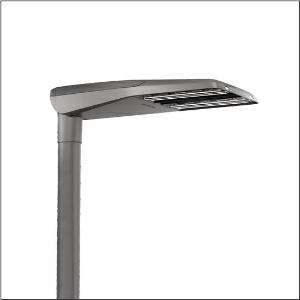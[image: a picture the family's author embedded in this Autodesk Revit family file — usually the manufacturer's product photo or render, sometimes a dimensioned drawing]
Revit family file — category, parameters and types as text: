
# Revit family: streetlight_sl_11_iq_midi___pc-l_5xc3e41e08me_b69f
name_source: partatom
category: Lighting Fixtures
units: mm (PartAtom-declared; Revit-internal decimal feet)

## family parameters
Cut with Voids When Loaded = No
Host = Face
Light Source = No
Part Type = Normal
Room Calculation Point = No
Round Connector Dimension = Use Diameter
Shared = No

## types (1)
- --- (1 x LED, 16220 lm, 124.7 W, 4000K)
    Apparent Load = 125 VA
    CIE Flux Codes = 37 73 96 100 100
    Color Rendering = 70
    Color Temperature = 4000K
    Default Elevation = 1800 mm
    Description = Streetlight SL 11 iQ midi, mast luminaire, primary light control with 3 zone facetted reflector, of plastic, silver coated, highly specular, primary optical cover: cover, of PMMA, transparent, light distribution: PC-L, light emission: direct distribution, primary light characteristic: asymmetric, left, installation type: post-top, side-entry, LED, High Power LED, rated luminous flux: 16.220lm, luminous efficacy: 130lm/W, light colour: 740, colour temperature: 4000K, control: optimised constant luminous flux control (CLO 2.0), Desk-Remote (wireless, voltage-free reading and setting of iQ features in the workshop via application-optimized NFC function/RFID function), Light-Fading, Smart-Wire, Night-Set, Lumen-Switch, Temp-Guard, Auto-Match, with cable H07RN-F 5x 1.5mm², mains connection: 230..240V, AC, 50/60Hz, connection cable pre-assembled, cable length: 12,5m, start of lifetime: 125W, end of service life: 132W, reduction: 57W, luminaire housing, of diecast aluminium, powder-coated, Siteco® metallic grey (DB 702S), please order mast flange separately, inclination adjustable without tools: 0°, 5°, 10°, 15° (post-top) | 0°, -5°, -10°, -15° (side-entry), sealing non-destructively replaceable, multi-level sealing system, length: 780mm, width: 376mm, height: 118mm, mast flange for spigot size: 42mm (side-entry): 5XC10008XM4, 60/48mm (side-entry/post-top): 5XC10108XM2, 76/60mm (side-entry/post-top): 5XC10108XM1, equipment: Power, protection rating (complete): IP66, insulation class (complete): insulation class II (safety insulation), certification: CE, ENEC, VDE, impact resistance: IK09, permissible operating ambient temperature for outdoor applications: -25..+50°C, standard-compliant lighting for roads and squares, Environmental Product Declaration (EPD) tested and certified by an independent institute, packaging unit: 1 piece

Light Distribution: PC-L
    Height = 118 mm
    Lamp = 1 x LED
    Lamp Light Flux = 16220 lm
    Lamp Power = 124.7 W
    Lamp count = 1
    Length = 780 mm
    Luminous efficacy = 130 lm/W
    Manufacturer = Siteco
    ModVariant = No
    Model = 5XC3E41E08ME
    Number of Poles = 1
    OnlyDefault = Yes
    Power Factor = 1
    Product Name = Streetlight SL 11 iQ midi | PC-L
    Product group = mast luminaire | pylon top
    ProductGroupID = 6100
    Protection Class = Protection class II
    Protection Degree = IP 66
    RLX_Detail_Level = 1
    RLX_Emergency_Light_Flux = 0 lm
    RLX_Emergency_Type = 0
    RLX_Emergency_Type_DB = No
    RlxData = <blob elided: 74617 chars, md5=6280aa3d>
    Socket = socket
    Standby Power = 0 W
    System Light Flux = 16220 lm
    System Power = 125 W
    Type Comments = factory setting: luminous flux: 100 % | dim-lin: 254 | 557 mA
    Type Image = l_1005960.jpg
    URL = http://relux.com
    VarID = @adj_131423
    Voltage = 0 V
    Weight = 0.00 kg
    Width = 376 mm

## geometry (parser evidence)
native form markers: Blend x4, Sweep x10
no freeform markers — native parametric forms only
